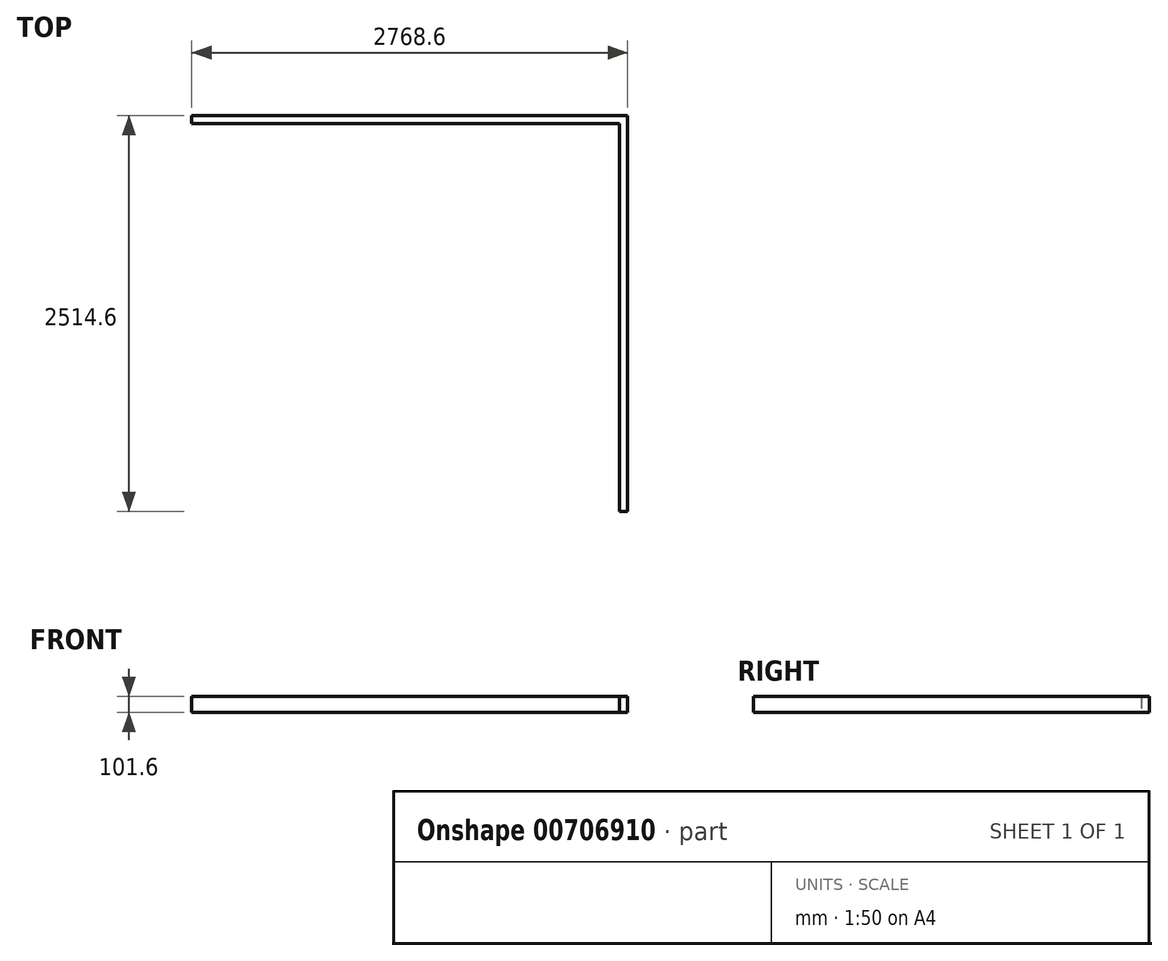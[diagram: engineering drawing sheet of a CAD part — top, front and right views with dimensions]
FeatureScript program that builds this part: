
annotation { "Feature Type Name" : "Feature", "Feature Type Description" : "" }
export const myFeature = defineFeature(function(context is Context, id is Id, definition is map)
    precondition{}
    {
        {
            var Q0;
            Q0=qCreatedBy(makeId("Top.planeOp"),FACE);
            var sketch = newSketch(context, id + "F0", { "sketchPlane" : qUnion([Q0])});
            skLineSegment(sketch, "E0.bottom", {"start": v(0, 0) * mm, "end": v(2768.6, 0) * mm});
            skLineSegment(sketch, "E0.top", {"start": v(0, 50.8) * mm, "end": v(2768.6, 50.8) * mm});
            skLineSegment(sketch, "E0.left", {"start": v(0, 0) * mm, "end": v(0, 50.8) * mm});
            skLineSegment(sketch, "E0.right", {"start": v(2768.6, 0) * mm, "end": v(2768.6, 50.8) * mm});
            skLineSegment(sketch, "E1.bottom", {"start": v(2768.6, 0) * mm, "end": v(2717.8, 0) * mm});
            skLineSegment(sketch, "E1.top", {"start": v(2768.6, -2463.8) * mm, "end": v(2717.8, -2463.8) * mm});
            skLineSegment(sketch, "E1.left", {"start": v(2768.6, 0) * mm, "end": v(2768.6, -2463.8) * mm});
            skLineSegment(sketch, "E1.right", {"start": v(2717.8, 0) * mm, "end": v(2717.8, -2463.8) * mm});
            skPoint(sketch, "E2.left.start.orphan", {"position": v(0, -962.56) * mm});
            skSolve(sketch);
        }
        {
            var Q0;
            Q0 = qSketchRegion(id + "F0", true);
            extrude(context, id + "F1", {"entities" : qUnion([Q0]), "depth" : 101.6 * mm, "offsetDistance" : 25.4 * mm});
        }
    });
